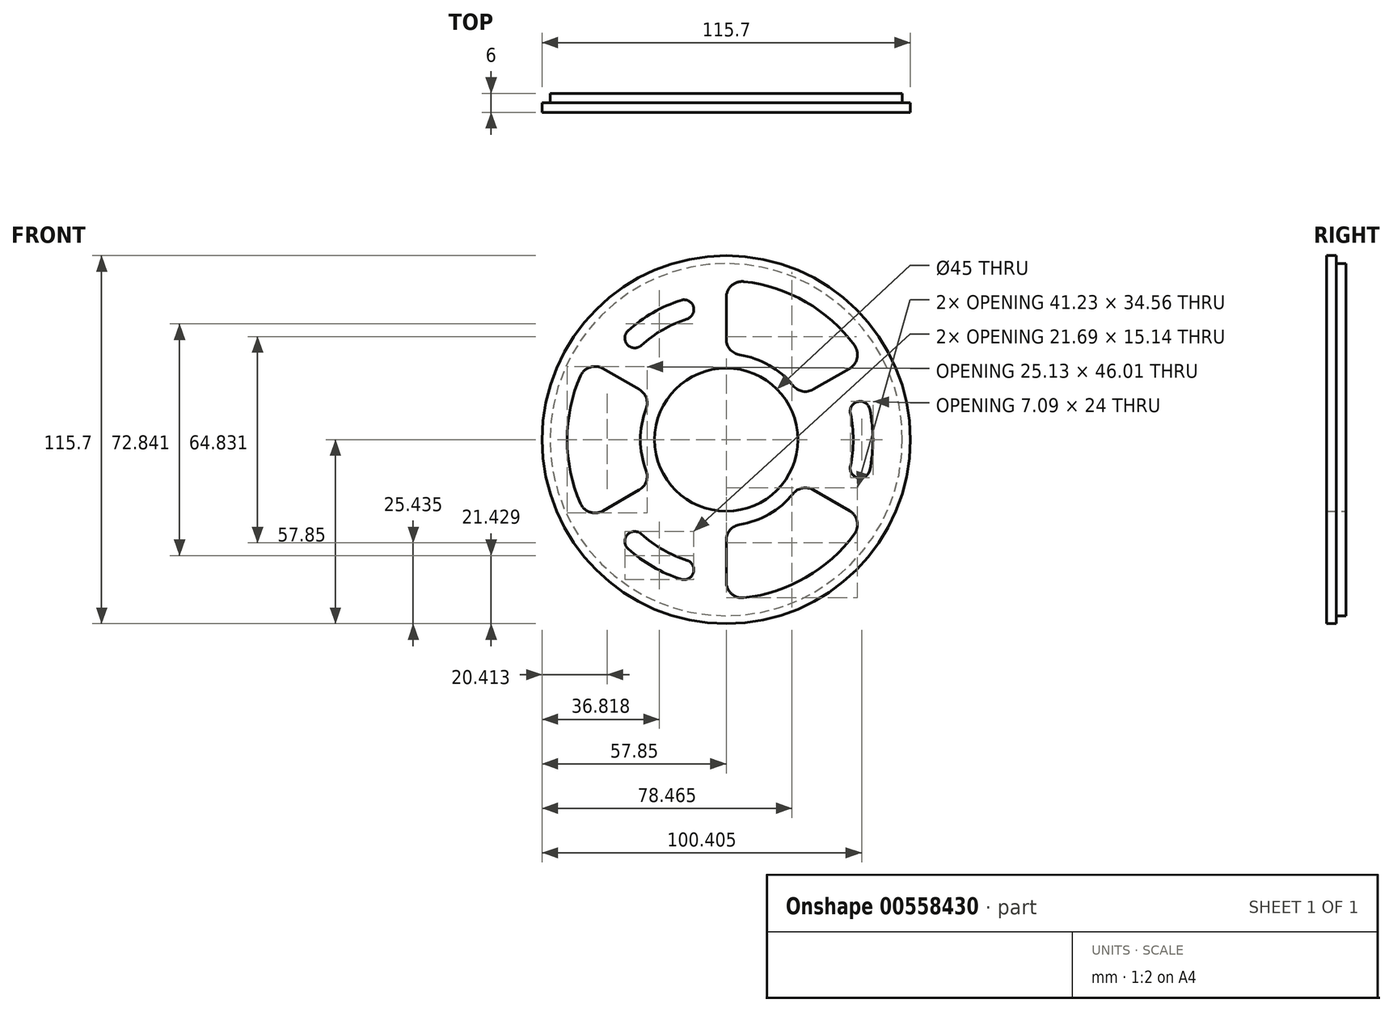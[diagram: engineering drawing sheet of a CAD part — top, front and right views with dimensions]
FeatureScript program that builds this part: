
annotation { "Feature Type Name" : "Feature", "Feature Type Description" : "" }
export const myFeature = defineFeature(function(context is Context, id is Id, definition is map)
    precondition{}
    {
        {
            var Q0;
            Q0=qCreatedBy(makeId("Front.planeOp"),FACE);
            var sketch = newSketch(context, id + "F0", { "sketchPlane" : qUnion([Q0])});
            skCircle(sketch, "E0", {"center": v(0, 0) * mm, "radius": 57.85 * mm});
            skCircle(sketch, "E1", {"center": v(0, 0) * mm, "radius": 22.5 * mm});
            skArc(sketch, "E2", {"start": v(45.1, -9.6) * mm, "mid": v(46.1, 0) * mm, "end": v(45.1, 9.6) * mm});
            skArc(sketch, "E3", {"start": v(39.03, -8.3) * mm, "mid": v(39.9, 0) * mm, "end": v(39.03, 8.3) * mm});
            skArc(sketch, "E4", {"start": v(45.1, 9.6) * mm, "mid": v(41.41, 11.98) * mm, "end": v(39.03, 8.3) * mm});
            skArc(sketch, "E5", {"start": v(39.03, -8.3) * mm, "mid": v(41.41, -11.98) * mm, "end": v(45.1, -9.6) * mm});
            skArc(sketch, "E6.MirrorCS", {"start": v(-14.23, 43.85) * mm, "mid": v(-10.33, 41.86) * mm, "end": v(-12.32, 37.95) * mm});
            skArc(sketch, "E7.MirrorCS", {"start": v(-30.86, 34.25) * mm, "mid": v(-23.05, 39.92) * mm, "end": v(-14.23, 43.85) * mm});
            skArc(sketch, "E8.MirrorCS", {"start": v(-26.7, 29.64) * mm, "mid": v(-19.95, 34.55) * mm, "end": v(-12.32, 37.95) * mm});
            skArc(sketch, "E9.MirrorCS", {"start": v(-26.7, 29.64) * mm, "mid": v(-31.08, 29.87) * mm, "end": v(-30.86, 34.25) * mm});
            skArc(sketch, "E10.MirrorCS", {"start": v(-14.23, -43.85) * mm, "mid": v(-23.05, -39.92) * mm, "end": v(-30.86, -34.25) * mm});
            skArc(sketch, "E11.MirrorCS", {"start": v(-12.32, -37.95) * mm, "mid": v(-19.95, -34.55) * mm, "end": v(-26.7, -29.64) * mm});
            skArc(sketch, "E12.MirrorCS", {"start": v(-30.86, -34.25) * mm, "mid": v(-31.08, -29.87) * mm, "end": v(-26.7, -29.64) * mm});
            skArc(sketch, "E13.MirrorCS", {"start": v(-12.32, -37.95) * mm, "mid": v(-10.33, -41.86) * mm, "end": v(-14.23, -43.85) * mm});
            skArc(sketch, "E14", {"start": v(-25.2, 9.68) * mm, "mid": v(-27, 0) * mm, "end": v(-25.2, -9.68) * mm});
            skArc(sketch, "E15", {"start": v(-45.81, 20.03) * mm, "mid": v(-50, 0) * mm, "end": v(-45.81, -20.03) * mm});
            skLineSegment(sketch, "E16.trimOffspring", {"start": v(-27.37, 15.8) * mm, "end": v(-38.73, 22.36) * mm});
            skLineSegment(sketch, "E17.trimOffspring", {"start": v(-27.37, -15.8) * mm, "end": v(-38.73, -22.36) * mm});
            skPoint(sketch, "E18.visualSharp", {"position": v(-23.38, 13.5) * mm});
            skArc(sketch, "E18.filletArc", {"start": v(-25.2, 9.68) * mm, "mid": v(-25.16, 13.14) * mm, "end": v(-27.37, 15.8) * mm});
            skPoint(sketch, "E19.visualSharp", {"position": v(-43.3, 25) * mm});
            skArc(sketch, "E19.filletArc", {"start": v(-38.73, 22.36) * mm, "mid": v(-42.8, 22.78) * mm, "end": v(-45.81, 20.03) * mm});
            skPoint(sketch, "E20.visualSharp", {"position": v(-43.3, -25) * mm});
            skArc(sketch, "E20.filletArc", {"start": v(-45.81, -20.03) * mm, "mid": v(-42.8, -22.78) * mm, "end": v(-38.73, -22.36) * mm});
            skPoint(sketch, "E21.visualSharp", {"position": v(-23.38, -13.5) * mm});
            skArc(sketch, "E21.filletArc", {"start": v(-27.37, -15.8) * mm, "mid": v(-25.16, -13.14) * mm, "end": v(-25.2, -9.68) * mm});
            skArc(sketch, "E22.MirrorCS", {"start": v(0, -31.6) * mm, "mid": v(1.2, -28.36) * mm, "end": v(4.22, -26.67) * mm});
            skArc(sketch, "E23.MirrorCS", {"start": v(20.99, -16.99) * mm, "mid": v(23.96, -15.22) * mm, "end": v(27.37, -15.8) * mm});
            skArc(sketch, "E24.MirrorCS", {"start": v(5.56, -49.7) * mm, "mid": v(1.67, -48.45) * mm, "end": v(0, -44.72) * mm});
            skPoint(sketch, "E25.MirrorP", {"position": v(23.38, -13.5) * mm});
            skLineSegment(sketch, "E26.MirrorCS", {"start": v(27.37, -15.8) * mm, "end": v(38.73, -22.36) * mm});
            skPoint(sketch, "E27.MirrorP", {"position": v(0, -50) * mm});
            skPoint(sketch, "E28.MirrorP", {"position": v(0, -27) * mm});
            skArc(sketch, "E29.MirrorCS", {"start": v(20.99, -16.99) * mm, "mid": v(13.5, -23.38) * mm, "end": v(4.22, -26.67) * mm});
            skLineSegment(sketch, "E30.MirrorCS", {"start": v(0, -31.6) * mm, "end": v(0, -44.72) * mm});
            skArc(sketch, "E31.MirrorCS", {"start": v(38.73, -22.36) * mm, "mid": v(41.12, -25.67) * mm, "end": v(40.26, -29.66) * mm});
            skArc(sketch, "E32.MirrorCS", {"start": v(40.26, -29.66) * mm, "mid": v(25, -43.3) * mm, "end": v(5.56, -49.7) * mm});
            skArc(sketch, "E33.MirrorCS", {"start": v(4.22, 26.67) * mm, "mid": v(1.2, 28.36) * mm, "end": v(0, 31.6) * mm});
            skArc(sketch, "E34.MirrorCS", {"start": v(0, 44.72) * mm, "mid": v(1.67, 48.45) * mm, "end": v(5.56, 49.7) * mm});
            skArc(sketch, "E35.MirrorCS", {"start": v(40.26, 29.66) * mm, "mid": v(41.12, 25.67) * mm, "end": v(38.73, 22.36) * mm});
            skArc(sketch, "E36.MirrorCS", {"start": v(4.22, 26.67) * mm, "mid": v(13.5, 23.38) * mm, "end": v(20.99, 16.99) * mm});
            skArc(sketch, "E37.MirrorCS", {"start": v(5.56, 49.7) * mm, "mid": v(25, 43.3) * mm, "end": v(40.26, 29.66) * mm});
            skPoint(sketch, "E38.MirrorP", {"position": v(0, 50) * mm});
            skLineSegment(sketch, "E39.MirrorCS", {"start": v(27.37, 15.8) * mm, "end": v(38.73, 22.36) * mm});
            skArc(sketch, "E40.MirrorCS", {"start": v(27.37, 15.8) * mm, "mid": v(23.96, 15.22) * mm, "end": v(20.99, 16.99) * mm});
            skLineSegment(sketch, "E41.MirrorCS", {"start": v(0, 31.6) * mm, "end": v(0, 44.72) * mm});
            skPoint(sketch, "E42.MirrorP", {"position": v(43.3, 25) * mm});
            skSolve(sketch);
        }
        {
            var Q0;
            Q0=makeQuery(id+"F0.imprint","IMPRINT",FACE,{"disambiguationData":[TD([[makeQuery(id+"F0.imprint","IMPRINT",EDGE,{"derivedFrom":sQuery(id+"F0.wireOp",EDGE,"E0")}),1.0]])]});
            extrude(context, id + "F1", {"entities" : qUnion([Q0]), "depth" : 6 * mm, "offsetDistance" : 25 * mm});
        }
        {
            var Q0;
            Q0=makeQuery(id+"F1.opExtrude","CAP_FACE",FACE,{"disambiguationData":[OSD([sQuery(id+"F0.wireOp",EDGE,"E0"),sQuery(id+"F0.wireOp",EDGE,"QBD5CPNR-eTBn-mDMN-URER-3Hg85SiTSXXa")])],"isStart":true});
            var sketch = newSketch(context, id + "F2", { "sketchPlane" : qUnion([Q0])});
            skCircle(sketch, "E43", {"center": v(0, 0) * mm, "radius": 55.35 * mm});
            skCircle(sketch, "E44", {"center": v(0, 0) * mm, "radius": 57.85 * mm});
            skSolve(sketch);
        }
        {
            var Q0;
            Q0=makeQuery(id+"F2.imprint","IMPRINT",FACE,{"disambiguationData":[TD([[makeQuery(id+"F2.imprint","IMPRINT",EDGE,{"derivedFrom":sQuery(id+"F2.wireOp",EDGE,"E43")}),-1.0]])]});
            extrude(context, id + "F3", {"entities" : qUnion([Q0]), "operationType" : NewBodyOperationType.REMOVE, "oppositeDirection" : true, "depth" : 3 * mm, "offsetDistance" : 25 * mm});
        }
    });
